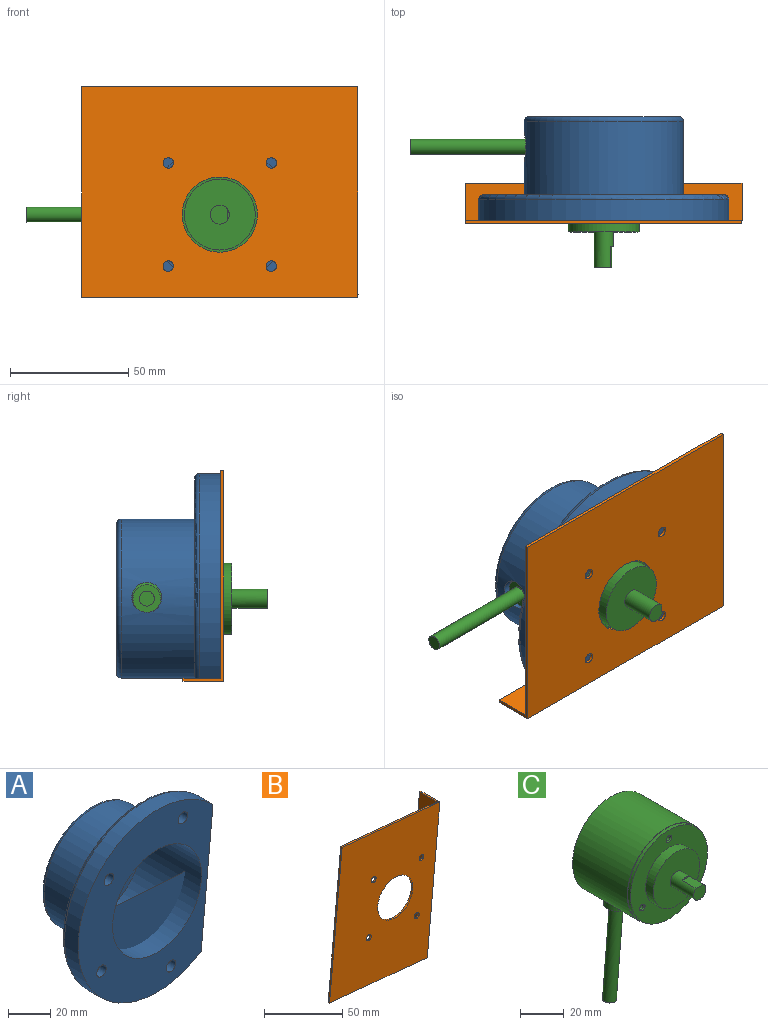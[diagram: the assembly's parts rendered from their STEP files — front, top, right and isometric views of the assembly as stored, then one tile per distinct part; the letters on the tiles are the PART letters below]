
ASSEMBLY  parts=3 mates=6
PART A: 43 faces, bbox 99x43.9x114.6 mm
  f0: plane 102.03x88.2mm, normal (0,1,0), area 3227.4mm2, adj f1,f8,f13,f14,f15,f16,f17,f18
  f1: plane 81.36x10.92mm, normal (1,0,-0.1), area 890.8mm2, adj f0,f5,f7,f42
  f2: cylinder r=3.17mm len=6.35mm, axis (0,1,0), area 103.9mm2, adj f7,f33
  f3: cylinder r=3.17mm len=6.35mm, axis (0,1,0), area 103.9mm2, adj f7,f19
  f4: cylinder r=3.17mm len=6.35mm, axis (0,1,0), area 103.9mm2, adj f7,f40
  f5: cylinder r=52.92mm len=105.84mm, axis (0,1,0), area 2156mm2, adj f1,f7,f42
  f6: cylinder r=3.17mm len=6.35mm, axis (0,1,0), area 103.9mm2, adj f7,f26
  f7: plane 105.84x90.35mm, normal (0,-1,0), area 4783.1mm2, adj f1,f2,f3,f4,f5,f6,f11
  f8: cylinder r=33.62mm len=67.23mm, axis (0,-1,0), area 6444.9mm2, adj f0,f12,f41
  f9: plane 63.42x63.42mm, normal (0,1,0), area 3159.3mm2, adj f41
  f10: plane 59.61x59.61mm, normal (0,-1,0), area 2791.2mm2, adj f11
  f11: cylinder r=29.81mm len=59.61mm, axis (0,-1,0), area 7388.5mm2, adj f7,f10,f12
  f12: cylinder r=6.35mm len=13.06mm, axis (-0.09,0,-1), area 153.6mm2, adj f8,f11
  f13: plane 6.4x5.72mm, normal (-0.95,0,-0.32), area 38.6mm2, adj f0,f14,f18,f19
  f14: plane 6.61x5.72mm, normal (-0.2,0,-0.98), area 38.6mm2, adj f0,f13,f15,f19
  f15: plane 5.72x5.05mm, normal (0.75,0,-0.66), area 38.6mm2, adj f0,f14,f16,f19
  f16: plane 6.4x5.72mm, normal (0.95,0,0.32), area 38.6mm2, adj f0,f15,f17,f19
  f17: plane 6.61x5.72mm, normal (0.2,0,0.98), area 38.6mm2, adj f0,f16,f18,f19
  f18: plane 5.72x5.05mm, normal (-0.75,0,0.66), area 38.6mm2, adj f0,f13,f17,f19
  f19: plane 13.22x12.8mm, normal (0,1,0), area 86.6mm2, adj f3,f13,f14,f15,f16,f17,f18
  f20: plane 6.75x5.72mm, normal (0.01,0,-1), area 38.6mm2, adj f0,f21,f25,f26
  f21: plane 5.87x5.72mm, normal (0.87,0,-0.49), area 38.6mm2, adj f0,f20,f22,f26
  f22: plane 5.82x5.72mm, normal (0.86,0,0.51), area 38.6mm2, adj f0,f21,f23,f26
  f23: plane 6.75x5.72mm, normal (-0.01,0,1), area 38.6mm2, adj f0,f22,f24,f26
  f24: plane 5.87x5.72mm, normal (-0.87,0,0.49), area 38.6mm2, adj f0,f23,f25,f26
  f25: plane 5.82x5.72mm, normal (-0.86,0,-0.51), area 38.6mm2, adj f0,f20,f24,f26
  f26: plane 13.49x11.73mm, normal (0,1,0), area 86.6mm2, adj f6,f20,f21,f22,f23,f24,f25
  f27: plane 6.43x5.72mm, normal (0.95,0,-0.3), area 38.6mm2, adj f0,f28,f32,f33
  f28: plane 5.72x4.98mm, normal (0.74,0,0.67), area 38.6mm2, adj f0,f27,f29,f33
  f29: plane 6.59x5.72mm, normal (-0.22,0,0.98), area 38.6mm2, adj f0,f28,f30,f33
  f30: plane 6.43x5.72mm, normal (-0.95,0,0.3), area 38.6mm2, adj f0,f29,f31,f33
  f31: plane 5.72x4.98mm, normal (-0.74,0,-0.67), area 38.6mm2, adj f0,f30,f32,f33
  f32: plane 6.59x5.72mm, normal (0.22,0,-0.98), area 38.6mm2, adj f0,f27,f31,f33
  f33: plane 13.18x12.86mm, normal (0,1,0), area 86.6mm2, adj f2,f27,f28,f29,f30,f31,f32
  f34: plane 6.7x5.72mm, normal (0.99,0,0.11), area 38.6mm2, adj f0,f35,f39,f40
  f35: plane 6.18x5.72mm, normal (0.4,0,0.92), area 38.6mm2, adj f0,f34,f36,f40
  f36: plane 5.72x5.43mm, normal (-0.59,0,0.8), area 38.6mm2, adj f0,f35,f37,f40
  f37: plane 6.7x5.72mm, normal (-0.99,0,-0.11), area 38.6mm2, adj f0,f36,f38,f40
  f38: plane 6.18x5.72mm, normal (-0.4,0,-0.92), area 38.6mm2, adj f0,f37,f39,f40
  f39: plane 5.72x5.43mm, normal (0.59,0,-0.8), area 38.6mm2, adj f0,f34,f38,f40
  f40: plane 13.41x12.37mm, normal (0,1,0), area 86.6mm2, adj f4,f34,f35,f36,f37,f38,f39
  f41: torus R=31.71mm, axis (0,-1,0), area 619mm2, adj f8,f9
  f42: torus R=51.02mm, axis (0,-1,0), area 709.6mm2, adj f0,f1,f5
PART B: 13 faces, bbox 99.8x17.1x125 mm
  f0: plane 124.9x98.56mm, normal (0,1,0), area 9389.9mm2, adj f2,f3,f4,f5,f7,f9,f10,f11
  f1: plane 116.39x17.15mm, normal (1,0,-0.1), area 2005mm2, adj f2,f4,f6,f8
  f2: plane 88.47x17.15mm, normal (0.1,0,1), area 133mm2, adj f0,f1,f3,f6,f7,f8
  f3: plane 116.39x11.36mm, normal (-1,0,0.1), area 148.5mm2, adj f0,f2,f4,f6
  f4: plane 88.47x17.15mm, normal (-0.1,0,-1), area 133mm2, adj f0,f1,f3,f6,f7,f8
  f5: cylinder r=15.9mm len=31.8mm, axis (0,1,0), area 126.9mm2, adj f0,f6
  f6: plane 125.02x99.83mm, normal (0,-1,0), area 9538.5mm2, adj f1,f2,f3,f4,f5,f9,f10,f11
  f7: plane 116.39x15.88mm, normal (-1,0,0.1), area 1856.5mm2, adj f0,f2,f4,f8
  f8: plane 116.51x12.62mm, normal (0,1,0), area 148.5mm2, adj f1,f2,f4,f7
  f9: cylinder r=2.22mm len=4.45mm, axis (0,-1,0), area 17.7mm2, adj f0,f6
  f10: cylinder r=2.22mm len=4.45mm, axis (0,-1,0), area 17.7mm2, adj f0,f6
  f11: cylinder r=2.22mm len=4.45mm, axis (0,-1,0), area 17.7mm2, adj f0,f6
  f12: cylinder r=2.22mm len=4.45mm, axis (0,-1,0), area 17.7mm2, adj f0,f6
PART C: 25 faces, bbox 50.2x56.8x107 mm
  f0: cylinder r=25.08mm len=50.17mm, axis (0,-1,0), area 5447.9mm2, adj f1,f2,f3,f22
  f1: cylinder r=25.08mm len=2.19mm, axis (0,-1,0), area 0.3mm2, adj f0,f2,f22
  f2: plane 50.17x50.17mm, normal (0,1,0), area 1976.5mm2, adj f0,f1
  f3: plane 50.17x50.17mm, normal (0,-1,0), area 43.8mm2, adj f0,f4
  f4: cylinder r=24.8mm len=49.61mm, axis (0,1,0), area 277.1mm2, adj f3,f5
  f5: plane 49.61x49.61mm, normal (0,-1,0), area 1199.4mm2, adj f4,f6,f18,f19,f20
  f6: cylinder r=14.99mm len=29.97mm, axis (0,1,0), area 454.4mm2, adj f5,f7
  f7: plane 29.97x29.97mm, normal (0,-1,0), area 655.3mm2, adj f6,f8
  f8: cylinder r=4mm len=14.99mm, axis (0,1,0), area 332.1mm2, adj f7,f9,f10,f11
  f9: plane 8x7.24mm, normal (0,-1,0), area 47.8mm2, adj f8,f10
  f10: plane 8.89x4.7mm, normal (0,0,1), area 41.8mm2, adj f8,f9,f11
  f11: plane 4.7x0.76mm, normal (0,-1,0), area 2.4mm2, adj f8,f10
  f12: cylinder r=1.21mm len=5.33mm, axis (0,-1,0), area 40.4mm2, adj f13,f18
  f13: plane 2.41x2.41mm, normal (0,-1,0), area 4.6mm2, adj f12
  f14: cylinder r=1.21mm len=5.33mm, axis (0,-1,0), area 40.4mm2, adj f15,f19
  f15: plane 2.41x2.41mm, normal (0,-1,0), area 4.6mm2, adj f14
  f16: cylinder r=1.21mm len=5.33mm, axis (0,-1,0), area 40.4mm2, adj f17,f20
  f17: plane 2.41x2.41mm, normal (0,-1,0), area 4.6mm2, adj f16
  f18: cone r=1.21mm half-angle=45deg, axis (0,-1,0), area 6.6mm2, adj f5,f12
  f19: cone r=1.21mm half-angle=45deg, axis (0,-1,0), area 6.6mm2, adj f5,f14
  f20: cone r=1.21mm half-angle=45deg, axis (0,-1,0), area 6.6mm2, adj f5,f16
  f21: plane 11.68x11.64mm, normal (-0.09,0,-1), area 75.6mm2, adj f22,f23
  f22: cylinder r=5.84mm len=12.23mm, axis (0.09,0,1), area 236.4mm2, adj f0,f1,f21
  f23: cylinder r=3.17mm len=51.16mm, axis (0.09,0,1), area 1013.4mm2, adj f21,f24
  f24: plane 6.35x6.33mm, normal (-0.09,0,-1), area 31.7mm2, adj f23
PLACE A rot(axis=(0,1,0),84.4deg) t=(0,-7.94,33.62)mm
PLACE B rot(axis=(0,1,0),84.4deg) t=(0,-6.16,33.62)mm
PLACE C rot(axis=(0,1,0),85deg) t=(0,-6.16,33.62)mm
MATE planar C.f0 <-> B.f0  axis (0,-1,0) through (0,-7.94,33.62)mm
MATE planar B.f7 <-> A.f1  axis (0,0,1) through (0,0,0)mm
MATE planar B.f0 <-> A.f7  axis (0,1,0) through (58.47,-7.94,43.81)mm
MATE cylindrical A.f11 <-> B.f5  axis (0,-1,0) through (0,12.13,33.62)mm
MATE parallel C.f23 <-> B.f4  axis (-1,0,0) through (-31.18,23.25,33.62)mm
MATE cylindrical C.f6 <-> B.f5  axis (0,-1,0) through (0,-7.94,33.62)mm
